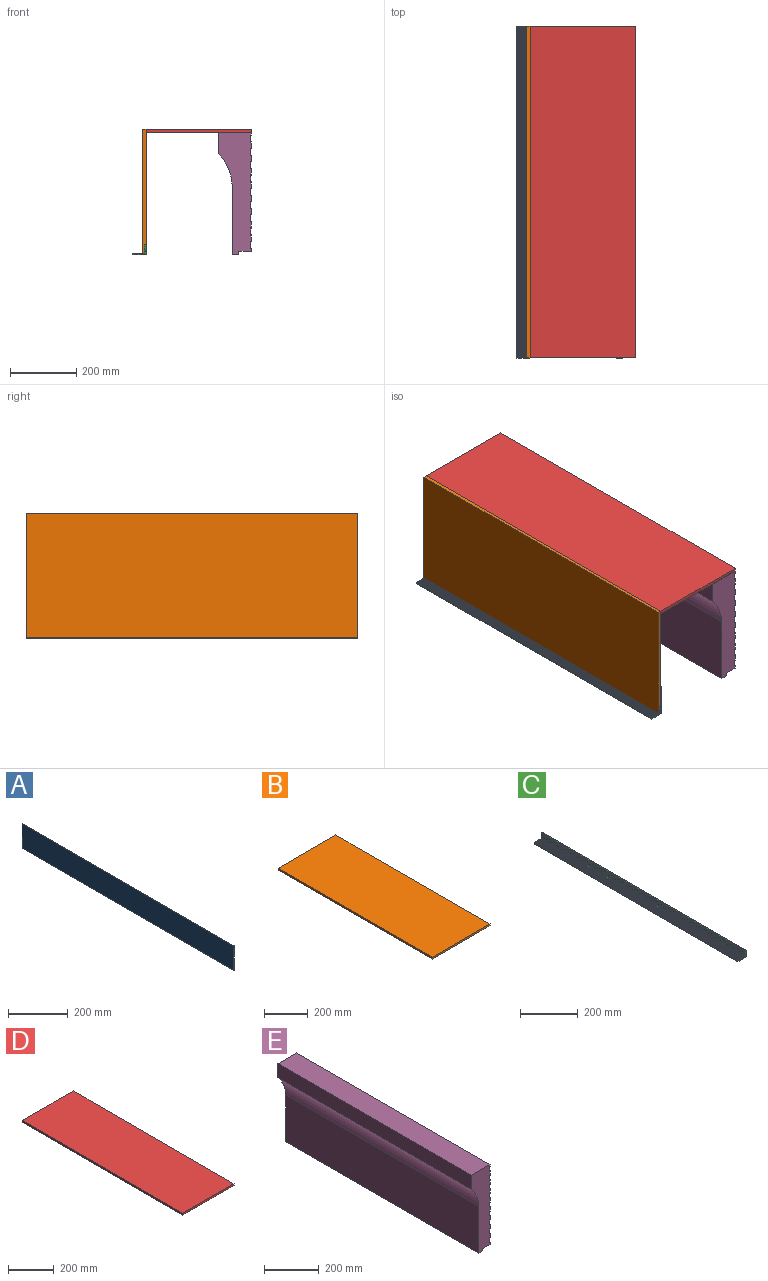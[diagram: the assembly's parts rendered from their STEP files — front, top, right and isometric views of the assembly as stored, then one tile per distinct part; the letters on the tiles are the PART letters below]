
ASSEMBLY  parts=5 mates=3
PART A: 6 faces, bbox 1.5x1000x100 mm
  f0: plane 1000x100mm, normal (-1,0,0), area 100000mm2, adj f1,f3,f4,f5
  f1: plane 1000x1.5mm, normal (0,0,-1), area 1500mm2, adj f0,f2,f4,f5
  f2: plane 1000x100mm, normal (1,0,0), area 100000mm2, adj f1,f3,f4,f5
  f3: plane 1000x1.5mm, normal (0,0,1), area 1500mm2, adj f0,f2,f4,f5
  f4: plane 100x1.5mm, normal (0,-1,0), area 150mm2, adj f0,f1,f2,f3
  f5: plane 100x1.5mm, normal (0,1,0), area 150mm2, adj f0,f1,f2,f3
PART B: 6 faces, bbox 375x1000x10 mm
  f0: plane 1000x10mm, normal (-1,0,0), area 10000mm2, adj f1,f3,f4,f5
  f1: plane 1000x375mm, normal (0,0,-1), area 375000mm2, adj f0,f2,f4,f5
  f2: plane 1000x10mm, normal (1,0,0), area 10000mm2, adj f1,f3,f4,f5
  f3: plane 1000x375mm, normal (0,0,1), area 375000mm2, adj f0,f2,f4,f5
  f4: plane 375x10mm, normal (0,-1,0), area 3750mm2, adj f0,f1,f2,f3
  f5: plane 375x10mm, normal (0,1,0), area 3750mm2, adj f0,f1,f2,f3
PART C: 87 faces, bbox 40x1000x30 mm
  f0: plane 1000x1.4mm, normal (0,0,1), area 1400mm2, adj f1,f84,f85,f86
  f1: cylinder r=0.3mm len=1000mm, axis (0,1,0), area 314.2mm2, adj f0,f2,f85,f86
  f2: cylinder r=0.3mm len=1000mm, axis (0,1,0), area 314.2mm2, adj f1,f3,f85,f86
  f3: plane 1000x3.06mm, normal (0,0,1), area 3060.8mm2, adj f2,f4,f85,f86
  f4: cylinder r=0.3mm len=1000mm, axis (0,1,0), area 314.2mm2, adj f3,f5,f85,f86
  f5: cylinder r=0.3mm len=1000mm, axis (0,1,0), area 314.2mm2, adj f4,f6,f85,f86
  f6: plane 1000x1.4mm, normal (0,0,1), area 1400mm2, adj f5,f7,f85,f86
  f7: cylinder r=0.3mm len=1000mm, axis (0,1,0), area 314.2mm2, adj f6,f8,f85,f86
  f8: cylinder r=0.3mm len=1000mm, axis (0,1,0), area 314.2mm2, adj f7,f9,f85,f86
  f9: plane 1000x3.06mm, normal (0,0,1), area 3060.8mm2, adj f8,f10,f85,f86
  f10: cylinder r=0.3mm len=1000mm, axis (0,1,0), area 314.2mm2, adj f9,f11,f85,f86
  f11: cylinder r=0.3mm len=1000mm, axis (0,1,0), area 314.2mm2, adj f10,f12,f85,f86
  f12: plane 1000x1.4mm, normal (0,0,1), area 1400mm2, adj f11,f13,f85,f86
  f13: cylinder r=0.3mm len=1000mm, axis (0,1,0), area 314.2mm2, adj f12,f14,f85,f86
  f14: cylinder r=0.3mm len=1000mm, axis (0,1,0), area 314.2mm2, adj f13,f15,f85,f86
  f15: plane 1000x3.06mm, normal (0,0,1), area 3060.8mm2, adj f14,f16,f85,f86
  f16: cylinder r=0.3mm len=1000mm, axis (0,1,0), area 314.2mm2, adj f15,f17,f85,f86
  f17: cylinder r=0.3mm len=1000mm, axis (0,1,0), area 314.2mm2, adj f16,f18,f85,f86
  f18: plane 1000x1.4mm, normal (0,0,1), area 1400mm2, adj f17,f19,f85,f86
  f19: cylinder r=0.3mm len=1000mm, axis (0,1,0), area 314.2mm2, adj f18,f20,f85,f86
  f20: cylinder r=0.3mm len=1000mm, axis (0,1,0), area 314.2mm2, adj f19,f21,f85,f86
  f21: plane 1000x3.06mm, normal (0,0,1), area 3060.8mm2, adj f20,f22,f85,f86
  f22: cylinder r=0.3mm len=1000mm, axis (0,1,0), area 314.2mm2, adj f21,f23,f85,f86
  f23: cylinder r=0.3mm len=1000mm, axis (0,1,0), area 314.2mm2, adj f22,f24,f85,f86
  f24: plane 1000x1.4mm, normal (0,0,1), area 1400mm2, adj f23,f25,f85,f86
  f25: cylinder r=0.3mm len=1000mm, axis (0,1,0), area 314.2mm2, adj f24,f26,f85,f86
  f26: cylinder r=0.3mm len=1000mm, axis (0,1,0), area 314.2mm2, adj f25,f27,f85,f86
  f27: plane 1000x3.06mm, normal (0,0,1), area 3060.8mm2, adj f26,f28,f85,f86
  f28: cylinder r=0.3mm len=1000mm, axis (0,1,0), area 314.2mm2, adj f27,f29,f85,f86
  f29: cylinder r=0.3mm len=1000mm, axis (0,1,0), area 314.2mm2, adj f28,f30,f85,f86
  f30: plane 1000x1.4mm, normal (0,0,1), area 1400mm2, adj f29,f31,f85,f86
  f31: cylinder r=0.3mm len=1000mm, axis (0,1,0), area 314.2mm2, adj f30,f32,f85,f86
  f32: cylinder r=0.3mm len=1000mm, axis (0,1,0), area 314.2mm2, adj f31,f33,f85,f86
  f33: plane 1000x0.98mm, normal (0,0,1), area 980.4mm2, adj f32,f34,f85,f86
  f34: cylinder r=0.3mm len=1000mm, axis (0,1,0), area 471.2mm2, adj f33,f35,f85,f86
  f35: plane 1000x4.4mm, normal (-1,0,0), area 4400mm2, adj f34,f36,f85,f86
  f36: cylinder r=0.3mm len=1000mm, axis (0,1,0), area 471.2mm2, adj f35,f37,f85,f86
  f37: plane 1000x11.1mm, normal (0,0,-1), area 11095.9mm2, adj f36,f38,f85,f86
  f38: cylinder r=0.5mm len=1000mm, axis (0,1,0), area 397.7mm2, adj f37,f39,f85,f86
  f39: cylinder r=0.5mm len=1000mm, axis (0,1,0), area 795.4mm2, adj f38,f40,f85,f86
  f40: cylinder r=0.5mm len=1000mm, axis (0,1,0), area 397.7mm2, adj f39,f41,f85,f86
  f41: plane 1000x1.37mm, normal (0,0,-1), area 1371.7mm2, adj f40,f42,f85,f86
  f42: cylinder r=0.5mm len=1000mm, axis (0,1,0), area 397.7mm2, adj f41,f43,f85,f86
  f43: cylinder r=0.5mm len=1000mm, axis (0,1,0), area 795.4mm2, adj f42,f44,f85,f86
  f44: cylinder r=0.5mm len=1000mm, axis (0,1,0), area 397.7mm2, adj f43,f45,f85,f86
  f45: plane 1000x11.78mm, normal (0,0,-1), area 11775.9mm2, adj f44,f46,f85,f86
  f46: cylinder r=0.3mm len=1000mm, axis (0,1,0), area 471.2mm2, adj f45,f47,f85,f86
  f47: plane 1000x1.1mm, normal (1,0,0), area 1100mm2, adj f46,f48,f85,f86
  f48: plane 1000x1.4mm, normal (0,0,-1), area 1400mm2, adj f47,f49,f85,f86
  f49: plane 1000x1.1mm, normal (-1,0,0), area 1100mm2, adj f48,f50,f85,f86
  f50: cylinder r=0.3mm len=1000mm, axis (0,1,0), area 471.2mm2, adj f49,f51,f85,f86
  f51: plane 1000x10.3mm, normal (0,0,-1), area 10300mm2, adj f50,f52,f85,f86
  f52: cylinder r=0.3mm len=1000mm, axis (0,1,0), area 471.2mm2, adj f51,f53,f85,f86
  f53: plane 1000x10.3mm, normal (1,0,0), area 10300mm2, adj f52,f54,f85,f86
  f54: cylinder r=0.3mm len=1000mm, axis (0,1,0), area 471.2mm2, adj f53,f55,f85,f86
  f55: plane 1000x1.1mm, normal (0,0,1), area 1100mm2, adj f54,f56,f85,f86
  f56: plane 1000x1.4mm, normal (1,0,0), area 1400mm2, adj f55,f57,f85,f86
  f57: plane 1000x1.1mm, normal (0,0,-1), area 1100mm2, adj f56,f58,f85,f86
  f58: cylinder r=0.3mm len=1000mm, axis (0,1,0), area 471.2mm2, adj f57,f59,f85,f86
  f59: plane 1000x17.1mm, normal (1,0,0), area 17100mm2, adj f58,f60,f85,f86
  f60: cylinder r=0.3mm len=1000mm, axis (0,1,0), area 471.2mm2, adj f59,f61,f85,f86
  f61: plane 1000x4.4mm, normal (0,0,1), area 4400mm2, adj f60,f62,f85,f86
  f62: cylinder r=0.3mm len=1000mm, axis (0,1,0), area 471.2mm2, adj f61,f63,f85,f86
  f63: plane 1000x3.48mm, normal (-1,0,0), area 3480.4mm2, adj f62,f64,f85,f86
  f64: cylinder r=0.3mm len=1000mm, axis (0,1,0), area 314.2mm2, adj f63,f65,f85,f86
  f65: cylinder r=0.3mm len=1000mm, axis (0,1,0), area 314.2mm2, adj f64,f66,f85,f86
  f66: plane 1000x1.4mm, normal (-1,0,0), area 1400mm2, adj f65,f67,f85,f86
  f67: cylinder r=0.3mm len=1000mm, axis (0,1,0), area 314.2mm2, adj f66,f68,f85,f86
  f68: cylinder r=0.3mm len=1000mm, axis (0,1,0), area 314.2mm2, adj f67,f69,f85,f86
  f69: plane 1000x5.06mm, normal (-1,0,0), area 5060.8mm2, adj f68,f70,f85,f86
  f70: cylinder r=0.3mm len=1000mm, axis (0,1,0), area 314.2mm2, adj f69,f71,f85,f86
  f71: cylinder r=0.3mm len=1000mm, axis (0,1,0), area 314.2mm2, adj f70,f72,f85,f86
  f72: plane 1000x1.4mm, normal (-1,0,0), area 1400mm2, adj f71,f73,f85,f86
  f73: cylinder r=0.3mm len=1000mm, axis (0,1,0), area 314.2mm2, adj f72,f74,f85,f86
  f74: cylinder r=0.3mm len=1000mm, axis (0,1,0), area 314.2mm2, adj f73,f75,f85,f86
  f75: plane 1000x5.06mm, normal (-1,0,0), area 5060.8mm2, adj f74,f76,f85,f86
  f76: cylinder r=0.3mm len=1000mm, axis (0,1,0), area 314.2mm2, adj f75,f77,f85,f86
  f77: cylinder r=0.3mm len=1000mm, axis (0,1,0), area 314.2mm2, adj f76,f78,f85,f86
  f78: plane 1000x1.4mm, normal (-1,0,0), area 1400mm2, adj f77,f79,f85,f86
  f79: cylinder r=0.3mm len=1000mm, axis (0,1,0), area 314.2mm2, adj f78,f80,f85,f86
  f80: cylinder r=0.3mm len=1000mm, axis (0,1,0), area 314.2mm2, adj f79,f81,f85,f86
  f81: plane 1000x3.78mm, normal (-1,0,0), area 3780.4mm2, adj f80,f82,f85,f86
  f82: plane 1000x3.78mm, normal (0,0,1), area 3780.4mm2, adj f81,f83,f85,f86
  f83: cylinder r=0.3mm len=1000mm, axis (0,1,0), area 314.2mm2, adj f82,f84,f85,f86
  f84: cylinder r=0.3mm len=1000mm, axis (0,1,0), area 314.2mm2, adj f0,f83,f85,f86
  f85: plane 40x30mm, normal (0,-1,0), area 325.7mm2, adj f0,f1,f2,f3,f4,f5,f6,f7
  f86: plane 40x30mm, normal (0,1,0), area 325.7mm2, adj f0,f1,f2,f3,f4,f5,f6,f7
PART D: 6 faces, bbox 317x1000x10 mm
  f0: plane 1000x10mm, normal (-1,0,0), area 10000mm2, adj f1,f3,f4,f5
  f1: plane 1000x317mm, normal (0,0,-1), area 317000mm2, adj f0,f2,f4,f5
  f2: plane 1000x10mm, normal (1,0,0), area 10000mm2, adj f1,f3,f4,f5
  f3: plane 1000x317mm, normal (0,0,1), area 317000mm2, adj f0,f2,f4,f5
  f4: plane 317x10mm, normal (0,-1,0), area 3170mm2, adj f0,f1,f2,f3
  f5: plane 317x10mm, normal (0,1,0), area 3170mm2, adj f0,f1,f2,f3
PART E: 46 faces, bbox 97.1x1000x368.5 mm
  f0: plane 1000x97.1mm, normal (0,0,1), area 97100mm2, adj f1,f43,f44,f45
  f1: plane 1000x63.5mm, normal (-1,0,0), area 63500mm2, adj f0,f2,f44,f45
  f2: cylinder r=157.8mm len=1000mm, axis (0,1,0), area 105640.8mm2, adj f1,f3,f44,f45
  f3: plane 1000x209.35mm, normal (-1,0,0), area 209347.8mm2, adj f2,f4,f44,f45
  f4: plane 1000x20.1mm, normal (0,0,-1), area 20100mm2, adj f3,f5,f44,f45
  f5: plane 1000x10mm, normal (1,0,0), area 10000mm2, adj f4,f6,f44,f45
  f6: plane 1000x37mm, normal (0,0,-1), area 37000mm2, adj f5,f7,f44,f45
  f7: plane 1000x10mm, normal (1,0,0), area 10000mm2, adj f6,f8,f44,f45
  f8: plane 1000x2mm, normal (-0.45,0,0.89), area 2236.1mm2, adj f7,f9,f44,f45
  f9: plane 1000x22mm, normal (1,0,0), area 22000mm2, adj f8,f10,f44,f45
  f10: plane 1000x2mm, normal (-0.45,0,-0.89), area 2236.1mm2, adj f9,f11,f44,f45
  f11: plane 1000x20mm, normal (1,0,0), area 20000mm2, adj f10,f12,f44,f45
  f12: plane 1000x2mm, normal (-0.45,0,0.89), area 2236.1mm2, adj f11,f13,f44,f45
  f13: plane 1000x22mm, normal (1,0,0), area 22000mm2, adj f12,f14,f44,f45
  f14: plane 1000x2mm, normal (-0.51,0,-0.86), area 2319.9mm2, adj f13,f15,f44,f45
  f15: plane 1000x20.18mm, normal (1,0,0), area 20175.7mm2, adj f14,f16,f44,f45
  f16: plane 1000x2mm, normal (-0.45,0,0.89), area 2236.1mm2, adj f15,f17,f44,f45
  f17: plane 1000x22mm, normal (1,0,0), area 22000mm2, adj f16,f18,f44,f45
  f18: plane 1000x2mm, normal (-0.45,0,-0.89), area 2236.1mm2, adj f17,f19,f44,f45
  f19: plane 1000x20mm, normal (1,0,0), area 20000mm2, adj f18,f20,f44,f45
  f20: plane 1000x2mm, normal (-0.45,0,0.89), area 2236.1mm2, adj f19,f21,f44,f45
  f21: plane 1000x22mm, normal (1,0,0), area 22000mm2, adj f20,f22,f44,f45
  f22: plane 1000x2mm, normal (-0.45,0,-0.89), area 2236.1mm2, adj f21,f23,f44,f45
  f23: plane 1000x20mm, normal (1,0,0), area 20000mm2, adj f22,f24,f44,f45
  f24: plane 1000x2mm, normal (-0.45,0,0.89), area 2236.1mm2, adj f23,f25,f44,f45
  f25: plane 1000x22mm, normal (1,0,0), area 22000mm2, adj f24,f26,f44,f45
  f26: plane 1000x2mm, normal (-0.45,0,-0.89), area 2236.1mm2, adj f25,f27,f44,f45
  f27: plane 1000x20mm, normal (1,0,0), area 20000mm2, adj f26,f28,f44,f45
  f28: plane 1000x2mm, normal (-0.45,0,0.89), area 2236.1mm2, adj f27,f29,f44,f45
  f29: plane 1000x22mm, normal (1,0,0), area 22000mm2, adj f28,f30,f44,f45
  f30: plane 1000x2mm, normal (-0.45,0,-0.89), area 2236.1mm2, adj f29,f31,f44,f45
  f31: plane 1000x20mm, normal (1,0,0), area 20000mm2, adj f30,f32,f44,f45
  f32: plane 1000x2mm, normal (-0.45,0,0.89), area 2236.1mm2, adj f31,f33,f44,f45
  f33: plane 1000x22mm, normal (1,0,0), area 22000mm2, adj f32,f34,f44,f45
  f34: plane 1000x2mm, normal (-0.45,0,-0.89), area 2236.1mm2, adj f33,f35,f44,f45
  f35: plane 1000x20mm, normal (1,0,0), area 20000mm2, adj f34,f36,f44,f45
  f36: plane 1000x2mm, normal (-0.45,0,0.89), area 2236.1mm2, adj f35,f37,f44,f45
  f37: plane 1000x22mm, normal (1,0,0), area 22000mm2, adj f36,f38,f44,f45
  f38: plane 1000x2mm, normal (-0.45,0,-0.89), area 2236.1mm2, adj f37,f39,f44,f45
  f39: plane 1000x20mm, normal (1,0,0), area 20000mm2, adj f38,f40,f44,f45
  f40: plane 1000x2mm, normal (-0.45,0,0.89), area 2236.1mm2, adj f39,f41,f44,f45
  f41: plane 1000x22mm, normal (1,0,0), area 22000mm2, adj f40,f42,f44,f45
  f42: plane 1000x2mm, normal (-0.45,0,-0.89), area 2236.1mm2, adj f41,f43,f44,f45
  f43: plane 1000x8.5mm, normal (1,0,0), area 8500mm2, adj f0,f42,f44,f45
  f44: plane 368.5x97.1mm, normal (0,-1,0), area 24137.8mm2, adj f0,f1,f2,f3,f4,f5,f6,f7
  f45: plane 368.5x97.1mm, normal (0,1,0), area 24137.8mm2, adj f0,f1,f2,f3,f4,f5,f6,f7
PLACE A t=(-500.6,245.34,-319.11)mm
PLACE B rot(axis=(0,-1,0),90deg) t=(-500.7,245.34,-315.91)mm
PLACE C t=(-520.6,245.34,-304.41)mm
PLACE D t=(-500.7,245.34,49.09)mm
PLACE E t=(-369.75,245.34,-109.41)mm
MATE fastened E.f44 <-> D.f4  axis (0,-1,0) through (-183.7,-754.66,49.09)mm
MATE fastened D.f4 <-> B.f4  axis (0,-1,0) through (-500.7,-754.66,59.09)mm
MATE fastened A.f4 <-> C.f85  axis (0,-1,0) through (-500.6,-754.66,-319.11)mm
